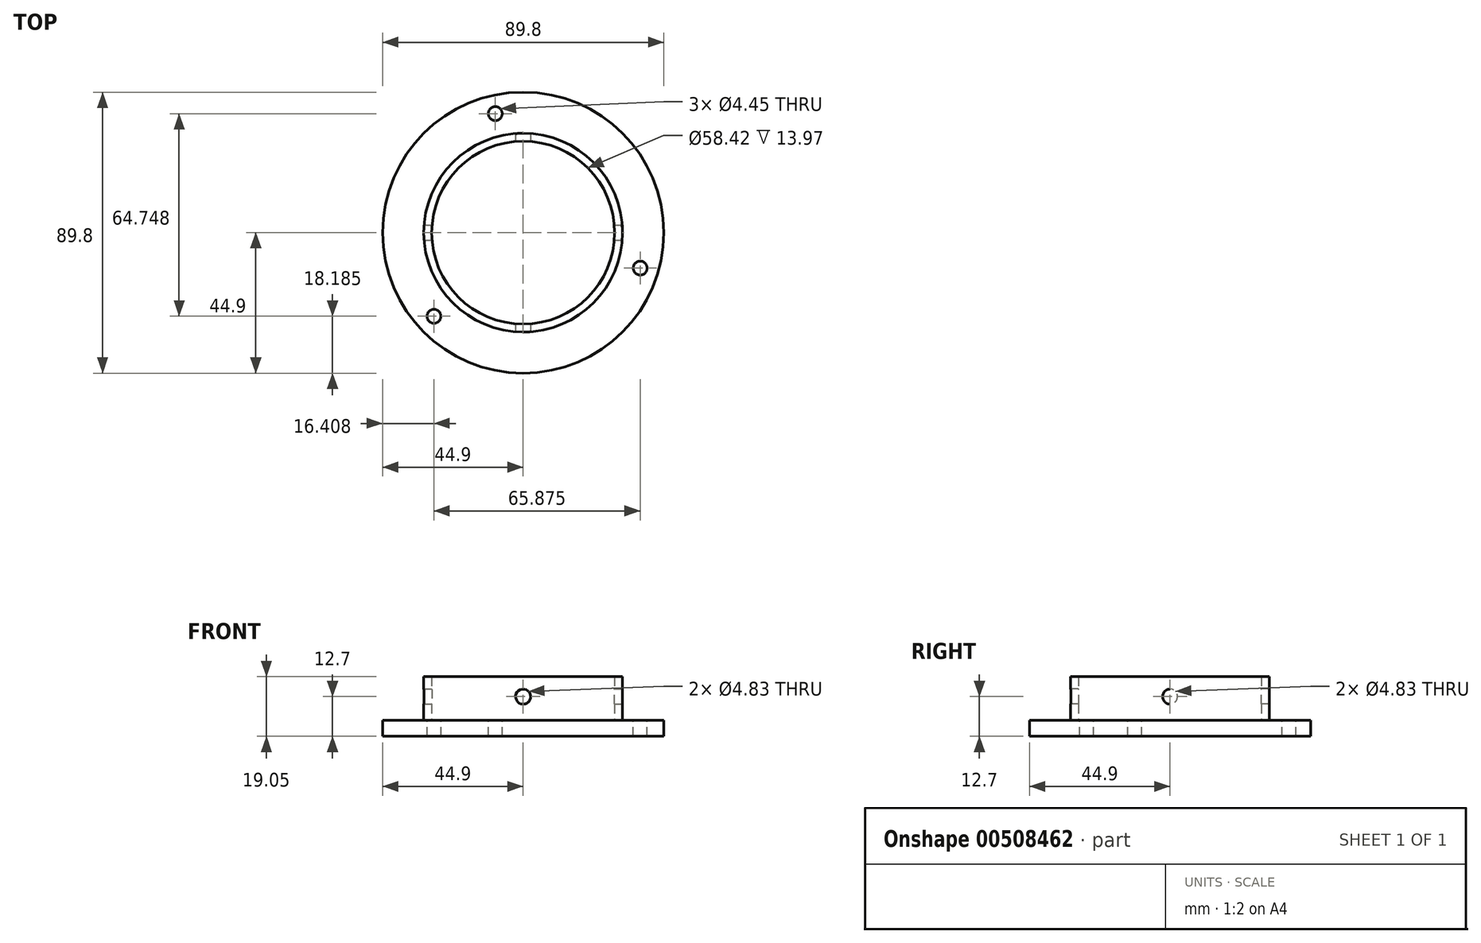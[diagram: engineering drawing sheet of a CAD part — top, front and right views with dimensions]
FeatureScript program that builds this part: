
annotation { "Feature Type Name" : "Feature", "Feature Type Description" : "" }
export const myFeature = defineFeature(function(context is Context, id is Id, definition is map)
    precondition{}
    {
        {
            var Q0;
            Q0=qCreatedBy(makeId("Top.planeOp"),FACE);
            var sketch = newSketch(context, id + "F0", { "sketchPlane" : qUnion([Q0])});
            skCircle(sketch, "E0", {"center": v(0, 0) * mm, "radius": 29.21 * mm});
            skCircle(sketch, "E1", {"center": v(0, 0) * mm, "radius": 31.75 * mm});
            skSolve(sketch);
        }
        {
            var Q0;
            Q0=qSketchRegion(id+"F0",true);
            extrude(context, id + "F1", {"entities" : qUnion([Q0]), "depth" : 13.97 * mm});
        }
        {
            var Q0;
            Q0=qCreatedBy(makeId("Top.planeOp"),FACE);
            var sketch = newSketch(context, id + "F2", { "sketchPlane" : qUnion([Q0])});
            skLineSegment(sketch, "E2.bottom", {"start": v(44.45, -2.54) * mm, "end": v(-44.45, -2.54) * mm});
            skLineSegment(sketch, "E2.top", {"start": v(44.45, 2.54) * mm, "end": v(-44.45, 2.54) * mm});
            skLineSegment(sketch, "E2.left", {"start": v(44.45, -2.54) * mm, "end": v(44.45, 2.54) * mm});
            skLineSegment(sketch, "E2.right", {"start": v(-44.45, -2.54) * mm, "end": v(-44.45, 2.54) * mm});
            skPoint(sketch, "E2.middle", {"position": v(0, 0) * mm});
            skLineSegment(sketch, "E3", {"start": v(-31.65, 2.54) * mm, "end": v(-31.65, -2.54) * mm});
            skLineSegment(sketch, "E4", {"start": v(31.65, 2.54) * mm, "end": v(31.65, -2.54) * mm});
            skSolve(sketch);
        }
        {
            var Q0;
            Q0=qCreatedBy(makeId("Top.planeOp"),FACE);
            var sketch = newSketch(context, id + "F3", { "sketchPlane" : qUnion([Q0])});
            skLineSegment(sketch, "E5.bottom", {"start": v(-60.23, 0) * mm, "end": v(63.71, 0) * mm});
            skLineSegment(sketch, "E5.top", {"start": v(-60.23, -73.9) * mm, "end": v(63.71, -73.9) * mm});
            skLineSegment(sketch, "E5.left", {"start": v(-60.23, 0) * mm, "end": v(-60.23, -73.9) * mm});
            skLineSegment(sketch, "E5.right", {"start": v(63.71, 0) * mm, "end": v(63.71, -73.9) * mm});
            skSolve(sketch);
        }
        {
            var Q0;
            Q0=qCreatedBy(makeId("Top.planeOp"),FACE);
            var sketch = newSketch(context, id + "F4", { "sketchPlane" : qUnion([Q0])});
            skCircle(sketch, "E6", {"center": v(0, 0) * mm, "radius": 44.9 * mm});
            skSolve(sketch);
        }
        {
            var Q0;
            Q0=qSketchRegion(id+"F4",true);
            extrude(context, id + "F5", {"entities" : qUnion([Q0]), "operationType" : NewBodyOperationType.ADD, "oppositeDirection" : true, "depth" : 5.08 * mm});
        }
        {
            var Q0;
            Q0=qCreatedBy(makeId("Front.planeOp"),FACE);
            var sketch = newSketch(context, id + "F6", { "sketchPlane" : qUnion([Q0])});
            skCircle(sketch, "E7", {"center": v(0, 7.62) * mm, "radius": 2.41 * mm});
            skSolve(sketch);
        }
        {
            var Q0;
            Q0=qSketchRegion(id+"F6",true);
            extrude(context, id + "F7", {"entities" : qUnion([Q0]), "operationType" : NewBodyOperationType.REMOVE, "endBound" : BoundingType.SYMMETRIC, "oppositeDirection" : true, "depth" : 76.2 * mm});
        }
        {
            var Q0;
            {var subQ6=sQuery(id+"F4.wireOp",EDGE,"E6");Q0=makeQuery(id+"FT47Tx4rUoxAfJh_1.opDraft","SPLIT",FACE,{"disambiguationData":[OD(1.0)],"derivedFrom":makeQuery(id+"F5.boolean.opBoolean","SPLIT",FACE,{"disambiguationData":[TD([makeQuery(id+"F1.opExtrude","SWEPT_FACE",FACE,{"disambiguationData":[OSD([sQuery(id+"F0.wireOp",EDGE,"E1")])]})])],"derivedFrom":makeQuery(id+"F5.opExtrude","CAP_FACE",FACE,{"disambiguationData":[OSD([subQ6])],"isStart":true})})});}
            var sketch = newSketch(context, id + "F8", { "sketchPlane" : qUnion([Q0])});
            skPoint(sketch, "E8", {"position": v(-8.9, 38.03) * mm});
            skPoint(sketch, "E9.1.0", {"position": v(-28.5, -26.72) * mm});
            skPoint(sketch, "E9.2.0", {"position": v(37.38, -11.32) * mm});
            skPoint(sketch, "E9.center", {"position": v(0, 0) * mm});
            skSolve(sketch);
        }
        {
            var Q0;
            Q0=sQuery(id+"F8.wireOp",VERTEX,"E8");
            var Q1;
            Q1=sQuery(id+"F8.wireOp",VERTEX,"E9.1.0");
            var Q2;
            Q2=sQuery(id+"F8.wireOp",VERTEX,"E9.2.0");
            var Q3;
            Q3=makeQuery(id+"F1.opExtrude","SWEPT_BODY",BODY,{"disambiguationData":[OSD([sQuery(id+"F0.wireOp",EDGE,"E0"),sQuery(id+"F0.wireOp",EDGE,"E1")])]});
            hole(context, id + "F9", {"style" : HoleStyle.SIMPLE, "endStyle" : HoleEndStyle.BLIND, "holeDiameter" : 4.44 * mm, "holeDepth" : 12.7 * mm, "tappedDepth" : 12.7 * mm, "tapClearance" : 3, "startFromSketch" : true, "locations" : qUnion([Q0, Q1, Q2]), "scope" : qUnion([Q3])});
        }
        {
            var Q0;
            Q0=qCreatedBy(makeId("Right.planeOp"),FACE);
            var sketch = newSketch(context, id + "F10", { "sketchPlane" : qUnion([Q0])});
            skCircle(sketch, "E10", {"center": v(0, 7.62) * mm, "radius": 2.41 * mm});
            skSolve(sketch);
        }
        {
            var Q0;
            Q0=qSketchRegion(id+"F10",true);
            extrude(context, id + "F11", {"entities" : qUnion([Q0]), "operationType" : NewBodyOperationType.REMOVE, "endBound" : BoundingType.SYMMETRIC, "oppositeDirection" : true, "depth" : 101.6 * mm});
        }
    });
